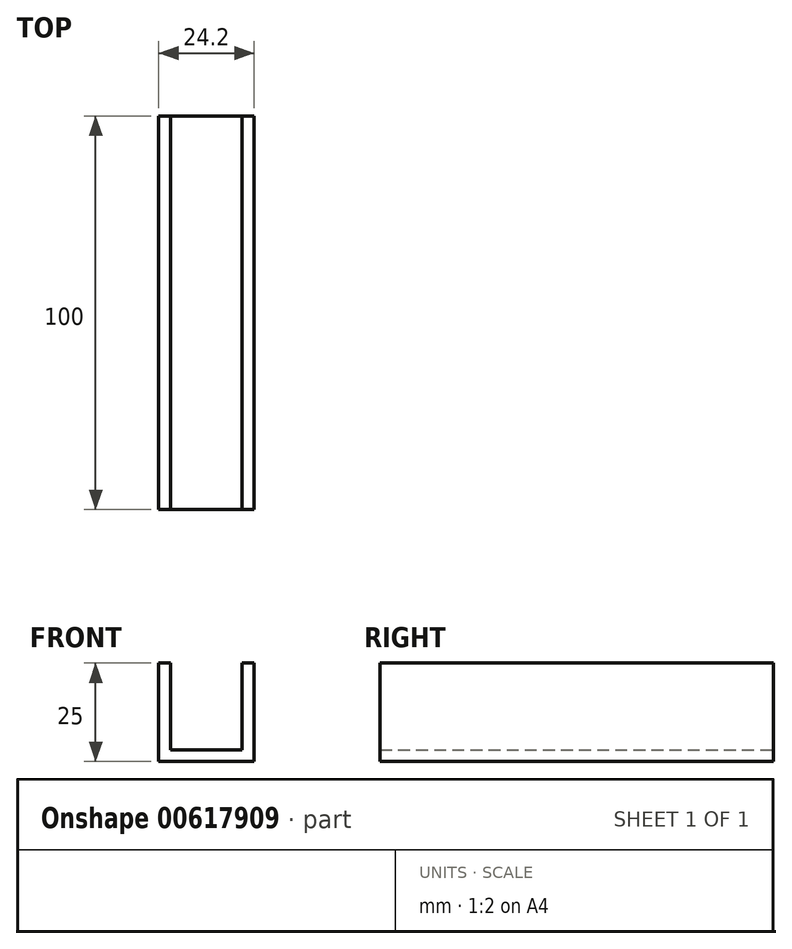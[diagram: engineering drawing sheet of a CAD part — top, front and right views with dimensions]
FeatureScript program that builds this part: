
annotation { "Feature Type Name" : "Feature", "Feature Type Description" : "" }
export const myFeature = defineFeature(function(context is Context, id is Id, definition is map)
    precondition{}
    {
        {
            var Q0;
            Q0=qCreatedBy(makeId("Front.planeOp"),FACE);
            var sketch = newSketch(context, id + "F0", { "sketchPlane" : qUnion([Q0])});
            skLineSegment(sketch, "E0", {"start": v(0, 0) * mm, "end": v(0, 25) * mm});
            skLineSegment(sketch, "E1", {"start": v(0, 25) * mm, "end": v(3, 25) * mm});
            skLineSegment(sketch, "E2", {"start": v(3, 25) * mm, "end": v(3, 3) * mm});
            skLineSegment(sketch, "E3", {"start": v(3, 3) * mm, "end": v(21.2, 3) * mm});
            skLineSegment(sketch, "E4", {"start": v(21.2, 3) * mm, "end": v(21.2, 25) * mm});
            skLineSegment(sketch, "E5", {"start": v(21.2, 25) * mm, "end": v(24.2, 25) * mm});
            skLineSegment(sketch, "E6", {"start": v(24.2, 25) * mm, "end": v(24.2, 0) * mm});
            skLineSegment(sketch, "E7", {"start": v(24.2, 0) * mm, "end": v(0, 0) * mm});
            skSolve(sketch);
        }
        {
            var Q0;
            Q0=makeQuery(id+"F0.imprint","IMPRINT",FACE,{"disambiguationData":[TD([[makeQuery(id+"F0.imprint","IMPRINT",EDGE,{"derivedFrom":sQuery(id+"F0.wireOp",EDGE,"E0")}),-1.0]])]});
            extrude(context, id + "F1", {"entities" : qUnion([Q0]), "depth" : 100 * mm, "offsetDistance" : 25 * mm});
        }
    });
